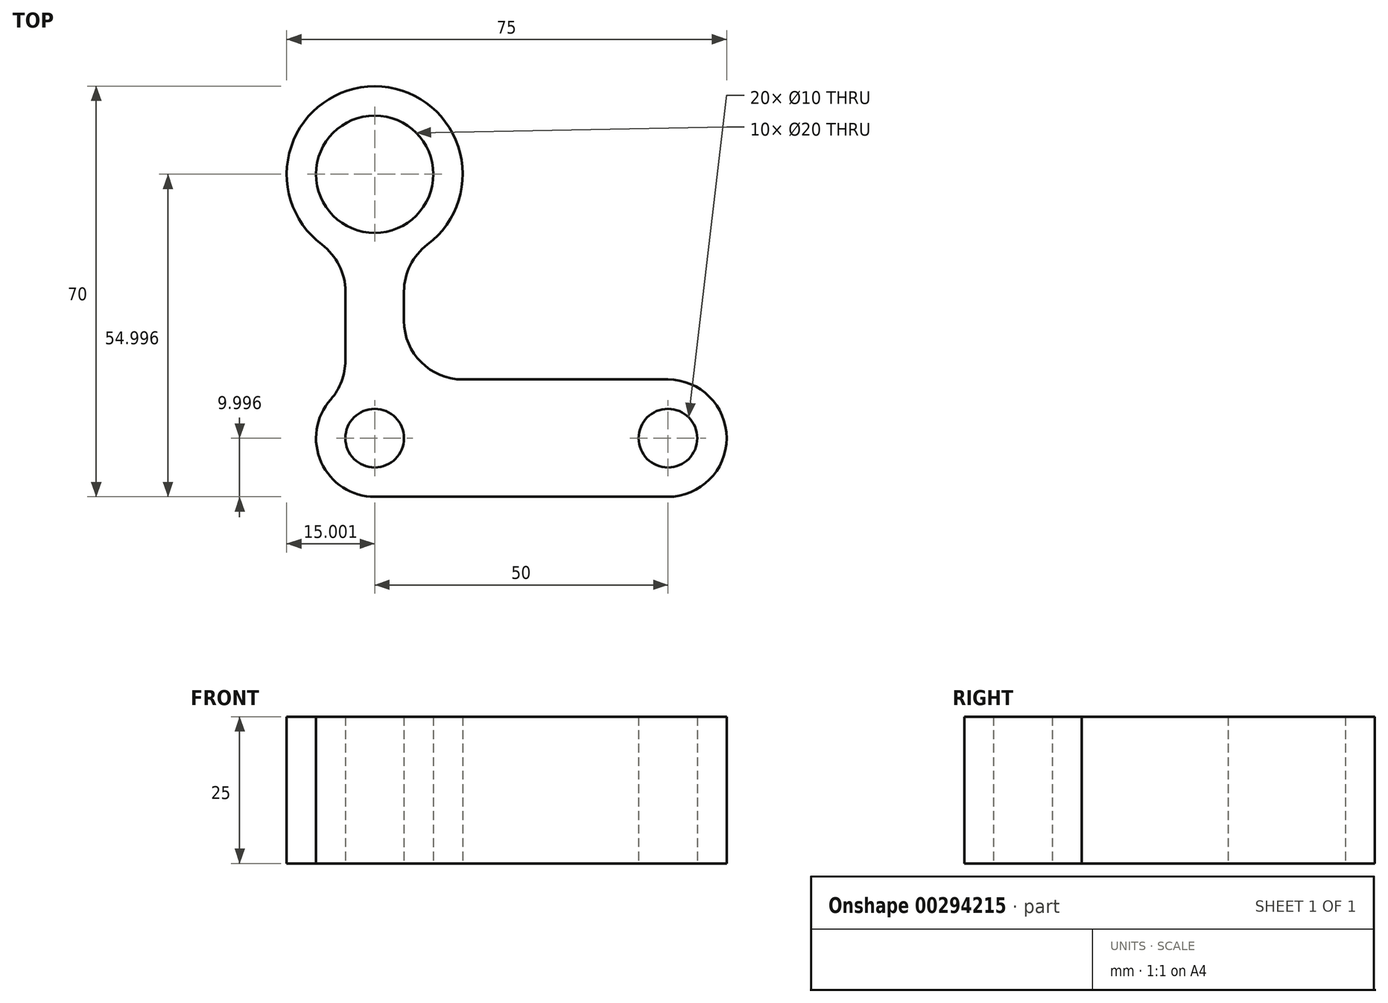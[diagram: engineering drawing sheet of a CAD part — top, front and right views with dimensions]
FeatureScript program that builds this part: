
annotation { "Feature Type Name" : "Feature", "Feature Type Description" : "" }
export const myFeature = defineFeature(function(context is Context, id is Id, definition is map)
    precondition{}
    {
        {
            var Q0;
            Q0=qCreatedBy(makeId("Top.planeOp"),FACE);
            var sketch = newSketch(context, id + "F0", { "sketchPlane" : qUnion([Q0])});
            skLineSegment(sketch, "E0", {"start": v(-23.2, -50.52) * mm, "end": v(26.8, -50.52) * mm});
            skLineSegment(sketch, "E1", {"start": v(-33.2, -40.52) * mm, "end": v(-33.2, -40.52) * mm});
            skLineSegment(sketch, "E2", {"start": v(-8.2, -30.52) * mm, "end": v(26.8, -30.52) * mm});
            skLineSegment(sketch, "E3", {"start": v(36.8, -40.52) * mm, "end": v(36.8, -40.52) * mm});
            skPoint(sketch, "E4.visualSharp", {"position": v(36.8, -30.52) * mm});
            skArc(sketch, "E4.filletArc", {"start": v(36.8, -40.52) * mm, "mid": v(33.87, -33.45) * mm, "end": v(26.8, -30.52) * mm});
            skPoint(sketch, "E5.visualSharp", {"position": v(36.8, -50.52) * mm});
            skArc(sketch, "E5.filletArc", {"start": v(26.8, -50.52) * mm, "mid": v(33.87, -47.6) * mm, "end": v(36.8, -40.52) * mm});
            skPoint(sketch, "E6.visualSharp", {"position": v(-33.2, -50.52) * mm});
            skArc(sketch, "E6.filletArc", {"start": v(-33.2, -40.52) * mm, "mid": v(-30.27, -47.6) * mm, "end": v(-23.2, -50.52) * mm});
            skPoint(sketch, "E7.visualSharp", {"position": v(-33.2, -30.52) * mm});
            skArc(sketch, "E7.filletArc", {"start": v(-30.7, -33.9) * mm, "mid": v(-32.55, -36.99) * mm, "end": v(-33.2, -40.52) * mm});
            skCircle(sketch, "E8", {"center": v(26.8, -40.52) * mm, "radius": 5 * mm});
            skCircle(sketch, "E9", {"center": v(-23.2, -40.52) * mm, "radius": 5 * mm});
            skCircle(sketch, "E10", {"center": v(-23.2, 4.48) * mm, "radius": 10 * mm});
            skLineSegment(sketch, "E11", {"start": v(-23.2, 19.48) * mm, "end": v(-23.2, 19.48) * mm});
            skLineSegment(sketch, "E12", {"start": v(-8.2, 4.48) * mm, "end": v(-8.2, 4.48) * mm});
            skLineSegment(sketch, "E13", {"start": v(-38.2, 4.48) * mm, "end": v(-38.2, 4.48) * mm});
            skPoint(sketch, "E14.visualSharp", {"position": v(-8.2, 19.48) * mm});
            skArc(sketch, "E14.filletArc", {"start": v(-8.2, 4.48) * mm, "mid": v(-12.6, 15.08) * mm, "end": v(-23.2, 19.48) * mm});
            skPoint(sketch, "E15.visualSharp", {"position": v(-38.2, 19.48) * mm});
            skArc(sketch, "E15.filletArc", {"start": v(-23.2, 19.48) * mm, "mid": v(-33.8, 15.08) * mm, "end": v(-38.2, 4.48) * mm});
            skLineSegment(sketch, "E16", {"start": v(-23.2, -10.52) * mm, "end": v(-23.2, -10.52) * mm});
            skPoint(sketch, "E17.visualSharp", {"position": v(-38.2, -10.52) * mm});
            skArc(sketch, "E17.filletArc", {"start": v(-38.2, 4.48) * mm, "mid": v(-36.62, -2.23) * mm, "end": v(-32.2, -7.52) * mm});
            skPoint(sketch, "E18.visualSharp", {"position": v(-8.2, -10.52) * mm});
            skArc(sketch, "E18.filletArc", {"start": v(-14.2, -7.52) * mm, "mid": v(-9.78, -2.23) * mm, "end": v(-8.2, 4.48) * mm});
            skLineSegment(sketch, "E19", {"start": v(-28.2, -19.16) * mm, "end": v(-28.2, -15.52) * mm});
            skLineSegment(sketch, "E20", {"start": v(-28.2, -15.52) * mm, "end": v(-28.2, -19.16) * mm});
            skLineSegment(sketch, "E21", {"start": v(-18.2, -19.16) * mm, "end": v(-18.2, -15.52) * mm});
            skLineSegment(sketch, "E22", {"start": v(-18.2, -15.52) * mm, "end": v(-18.2, -19.16) * mm});
            skLineSegment(sketch, "E23", {"start": v(-28.2, -19.16) * mm, "end": v(-28.2, -27.3) * mm});
            skLineSegment(sketch, "E24", {"start": v(-18.2, -19.16) * mm, "end": v(-18.2, -20.52) * mm});
            skPoint(sketch, "E25.visualSharp", {"position": v(-18.2, -9.67) * mm});
            skArc(sketch, "E25.filletArc", {"start": v(-14.2, -7.52) * mm, "mid": v(-17.14, -11.05) * mm, "end": v(-18.2, -15.52) * mm});
            skPoint(sketch, "E26.visualSharp", {"position": v(-28.2, -9.67) * mm});
            skArc(sketch, "E26.filletArc", {"start": v(-28.2, -15.52) * mm, "mid": v(-29.25, -11.05) * mm, "end": v(-32.2, -7.52) * mm});
            skPoint(sketch, "E27.visualSharp", {"position": v(-18.2, -30.52) * mm});
            skArc(sketch, "E27.filletArc", {"start": v(-18.2, -20.52) * mm, "mid": v(-15.27, -27.6) * mm, "end": v(-8.2, -30.52) * mm});
            skPoint(sketch, "E28.visualSharp", {"position": v(-28.2, -31.86) * mm});
            skArc(sketch, "E28.filletArc", {"start": v(-30.7, -33.9) * mm, "mid": v(-28.84, -30.83) * mm, "end": v(-28.2, -27.3) * mm});
            skSolve(sketch);
        }
        {
            var Q0;
            Q0 = qSketchRegion(id + "F0", true);
            extrude(context, id + "F1", {"entities" : qUnion([Q0]), "depth" : 25 * mm});
        }
    });
